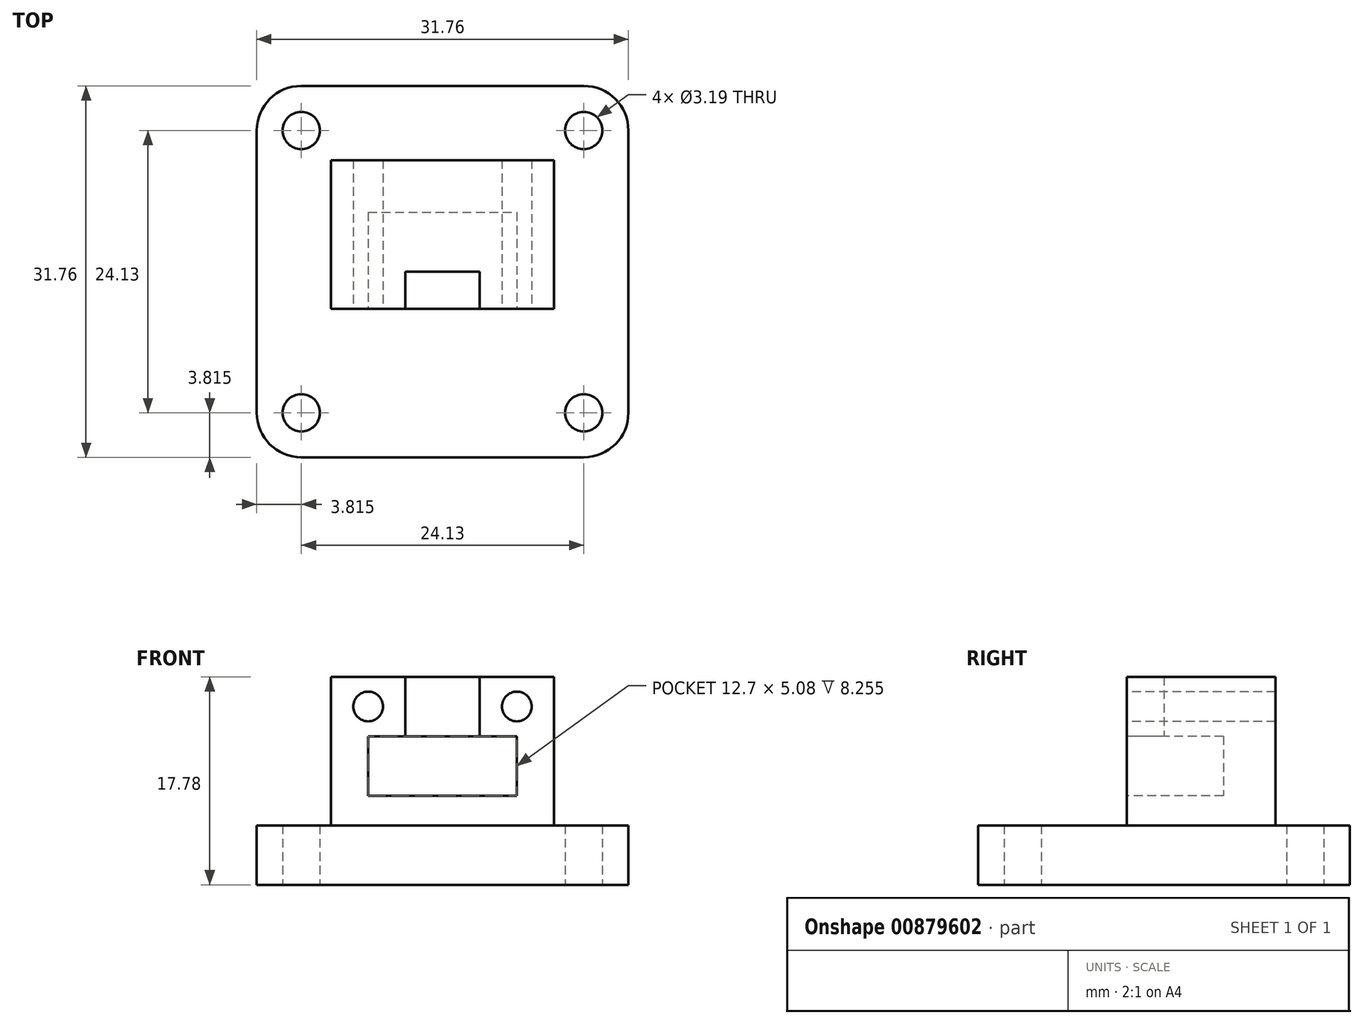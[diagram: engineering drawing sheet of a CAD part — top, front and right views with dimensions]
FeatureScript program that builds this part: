
annotation { "Feature Type Name" : "Feature", "Feature Type Description" : "" }
export const myFeature = defineFeature(function(context is Context, id is Id, definition is map)
    precondition{}
    {
        {
            var Q0;
            Q0=qCreatedBy(makeId("Top.planeOp"),FACE);
            var sketch = newSketch(context, id + "F0", { "sketchPlane" : qUnion([Q0])});
            skLineSegment(sketch, "E0.bottom", {"start": v(12.07, 15.88) * mm, "end": v(-12.07, 15.87) * mm});
            skLineSegment(sketch, "E0.top", {"start": v(12.07, -15.88) * mm, "end": v(-12.07, -15.88) * mm});
            skLineSegment(sketch, "E0.left", {"start": v(15.87, 12.06) * mm, "end": v(15.88, -12.06) * mm});
            skLineSegment(sketch, "E0.right", {"start": v(-15.88, 12.06) * mm, "end": v(-15.87, -12.06) * mm});
            skPoint(sketch, "E0.middle", {"position": v(0, 0) * mm});
            skCircle(sketch, "E1", {"center": v(-12.07, 12.06) * mm, "radius": 1.6 * mm});
            skPoint(sketch, "E2.visualSharp", {"position": v(-15.88, 15.88) * mm});
            skArc(sketch, "E2.filletArc", {"start": v(-12.07, 15.87) * mm, "mid": v(-14.76, 14.76) * mm, "end": v(-15.88, 12.06) * mm});
            skArc(sketch, "E3.MirrorCS", {"start": v(12.07, 15.87) * mm, "mid": v(14.76, 14.76) * mm, "end": v(15.88, 12.06) * mm});
            skCircle(sketch, "E4.MirrorC", {"center": v(12.07, 12.06) * mm, "radius": 1.6 * mm});
            skPoint(sketch, "E5.orphan", {"position": v(15.88, 15.88) * mm});
            skArc(sketch, "E6.MirrorCS", {"start": v(-12.07, -15.87) * mm, "mid": v(-14.76, -14.76) * mm, "end": v(-15.88, -12.06) * mm});
            skCircle(sketch, "E7.MirrorC", {"center": v(-12.07, -12.06) * mm, "radius": 1.6 * mm});
            skArc(sketch, "E8.MirrorCS", {"start": v(12.07, -15.87) * mm, "mid": v(14.76, -14.76) * mm, "end": v(15.88, -12.06) * mm});
            skCircle(sketch, "E9.MirrorC", {"center": v(12.07, -12.06) * mm, "radius": 1.6 * mm});
            skPoint(sketch, "E10.orphan", {"position": v(15.87, -15.87) * mm});
            skPoint(sketch, "E11.orphan", {"position": v(-15.87, -15.87) * mm});
            skSolve(sketch);
        }
        {
            var Q0;
            Q0 = qSketchRegion(id + "F0", true);
            extrude(context, id + "F1", {"entities" : qUnion([Q0]), "depth" : 5.08 * mm, "offsetDistance" : 25.4 * mm});
        }
        {
            var Q0;
            Q0=makeQuery(id+"F1.opExtrude","CAP_FACE",FACE,{"disambiguationData":[OSD([sQuery(id+"F0.wireOp",EDGE,"E0.bottom"),sQuery(id+"F0.wireOp",EDGE,"E0.top"),sQuery(id+"F0.wireOp",EDGE,"E0.left"),sQuery(id+"F0.wireOp",EDGE,"E0.right"),sQuery(id+"F0.wireOp",EDGE,"E1"),sQuery(id+"F0.wireOp",EDGE,"E2.filletArc"),sQuery(id+"F0.wireOp",EDGE,"E3.MirrorCS"),sQuery(id+"F0.wireOp",EDGE,"E4.MirrorC"),sQuery(id+"F0.wireOp",EDGE,"E6.MirrorCS"),sQuery(id+"F0.wireOp",EDGE,"E7.MirrorC"),sQuery(id+"F0.wireOp",EDGE,"E8.MirrorCS"),sQuery(id+"F0.wireOp",EDGE,"E9.MirrorC")])],"isStart":false});
            var sketch = newSketch(context, id + "F2", { "sketchPlane" : qUnion([Q0])});
            skPoint(sketch, "E12.middle", {"position": v(0, 0) * mm});
            skLineSegment(sketch, "E13.bottom", {"start": v(-9.53, -3.18) * mm, "end": v(9.53, -3.18) * mm});
            skLineSegment(sketch, "E13.top", {"start": v(-9.53, 9.53) * mm, "end": v(9.52, 9.53) * mm});
            skLineSegment(sketch, "E13.left", {"start": v(-9.52, -3.18) * mm, "end": v(-9.53, 9.53) * mm});
            skLineSegment(sketch, "E13.right", {"start": v(9.53, -3.18) * mm, "end": v(9.52, 9.53) * mm});
            skPoint(sketch, "E13.middle", {"position": v(0, 3.18) * mm});
            skSolve(sketch);
        }
        {
            var Q0;
            Q0 = qSketchRegion(id + "F2", true);
            extrude(context, id + "F3", {"entities" : qUnion([Q0]), "operationType" : NewBodyOperationType.ADD, "depth" : 12.7 * mm, "offsetDistance" : 25.4 * mm});
        }
        {
            var Q0;
            Q0=makeQuery(id+"F3.opExtrude","SWEPT_FACE",FACE,{"disambiguationData":[OSD([sQuery(id+"F2.wireOp",EDGE,"E13.bottom")])]});
            var sketch = newSketch(context, id + "F4", { "sketchPlane" : qUnion([Q0])});
            skLineSegment(sketch, "E14.bottom", {"start": v(-3.18, 17.78) * mm, "end": v(3.18, 17.78) * mm});
            skLineSegment(sketch, "E14.top", {"start": v(-3.18, 12.7) * mm, "end": v(3.18, 12.7) * mm});
            skLineSegment(sketch, "E14.left", {"start": v(-3.18, 17.78) * mm, "end": v(-3.18, 12.7) * mm});
            skLineSegment(sketch, "E14.right", {"start": v(3.18, 17.78) * mm, "end": v(3.18, 12.7) * mm});
            skLineSegment(sketch, "E15.bottom", {"start": v(-6.35, 12.7) * mm, "end": v(6.35, 12.7) * mm});
            skLineSegment(sketch, "E15.top", {"start": v(-6.35, 7.62) * mm, "end": v(6.35, 7.62) * mm});
            skLineSegment(sketch, "E15.left", {"start": v(-6.35, 12.7) * mm, "end": v(-6.35, 7.62) * mm});
            skLineSegment(sketch, "E15.right", {"start": v(6.35, 12.7) * mm, "end": v(6.35, 7.62) * mm});
            skSolve(sketch);
        }
        {
            var Q0;
            Q0 = qSketchRegion(id + "F4", true);
            extrude(context, id + "F5", {"entities" : qUnion([Q0]), "operationType" : NewBodyOperationType.REMOVE, "oppositeDirection" : true, "depth" : 3.17 * mm, "offsetDistance" : 25.4 * mm});
        }
        {
            var Q0;
            Q0=makeQuery(id+"F5.boolean.opBoolean","COPY",FACE,{"derivedFrom":makeQuery(id+"F5.opExtrude","CAP_FACE",FACE,{"disambiguationData":[OSD([sQuery(id+"F4.wireOp",EDGE,"E14.bottom"),sQuery(id+"F4.wireOp",EDGE,"E14.left"),sQuery(id+"F4.wireOp",EDGE,"E14.right"),sQuery(id+"F4.wireOp",EDGE,"E15.bottom"),sQuery(id+"F4.wireOp",EDGE,"E15.top"),sQuery(id+"F4.wireOp",EDGE,"E15.left"),sQuery(id+"F4.wireOp",EDGE,"E15.right")])],"isStart":false})});
            var sketch = newSketch(context, id + "F6", { "sketchPlane" : qUnion([Q0])});
            skLineSegment(sketch, "E16.bottom", {"start": v(-6.35, 7.62) * mm, "end": v(6.35, 7.62) * mm});
            skLineSegment(sketch, "E16.top", {"start": v(-6.35, 12.7) * mm, "end": v(6.35, 12.7) * mm});
            skLineSegment(sketch, "E16.left", {"start": v(-6.35, 7.62) * mm, "end": v(-6.35, 12.7) * mm});
            skLineSegment(sketch, "E16.right", {"start": v(6.35, 7.62) * mm, "end": v(6.35, 12.7) * mm});
            skSolve(sketch);
        }
        {
            var Q0;
            Q0 = qSketchRegion(id + "F6", true);
            extrude(context, id + "F7", {"entities" : qUnion([Q0]), "operationType" : NewBodyOperationType.REMOVE, "oppositeDirection" : true, "depth" : 5.08 * mm, "offsetDistance" : 25.4 * mm});
        }
        {
            var Q0;
            Q0=makeQuery(id+"F3.opExtrude","SWEPT_FACE",FACE,{"disambiguationData":[OSD([sQuery(id+"F2.wireOp",EDGE,"E13.bottom")])]});
            var sketch = newSketch(context, id + "F8", { "sketchPlane" : qUnion([Q0])});
            skCircle(sketch, "E17", {"center": v(-6.35, 15.24) * mm, "radius": 1.27 * mm});
            skPoint(sketch, "E17.centerSnap0", {"position": v(-3.18, 15.24) * mm});
            skCircle(sketch, "E18.MirrorC", {"center": v(6.35, 15.24) * mm, "radius": 1.27 * mm});
            skSolve(sketch);
        }
        {
            var Q0;
            Q0 = qSketchRegion(id + "F8", true);
            extrude(context, id + "F9", {"entities" : qUnion([Q0]), "operationType" : NewBodyOperationType.REMOVE, "oppositeDirection" : true, "depth" : 12.7 * mm, "offsetDistance" : 25.4 * mm});
        }
    });
